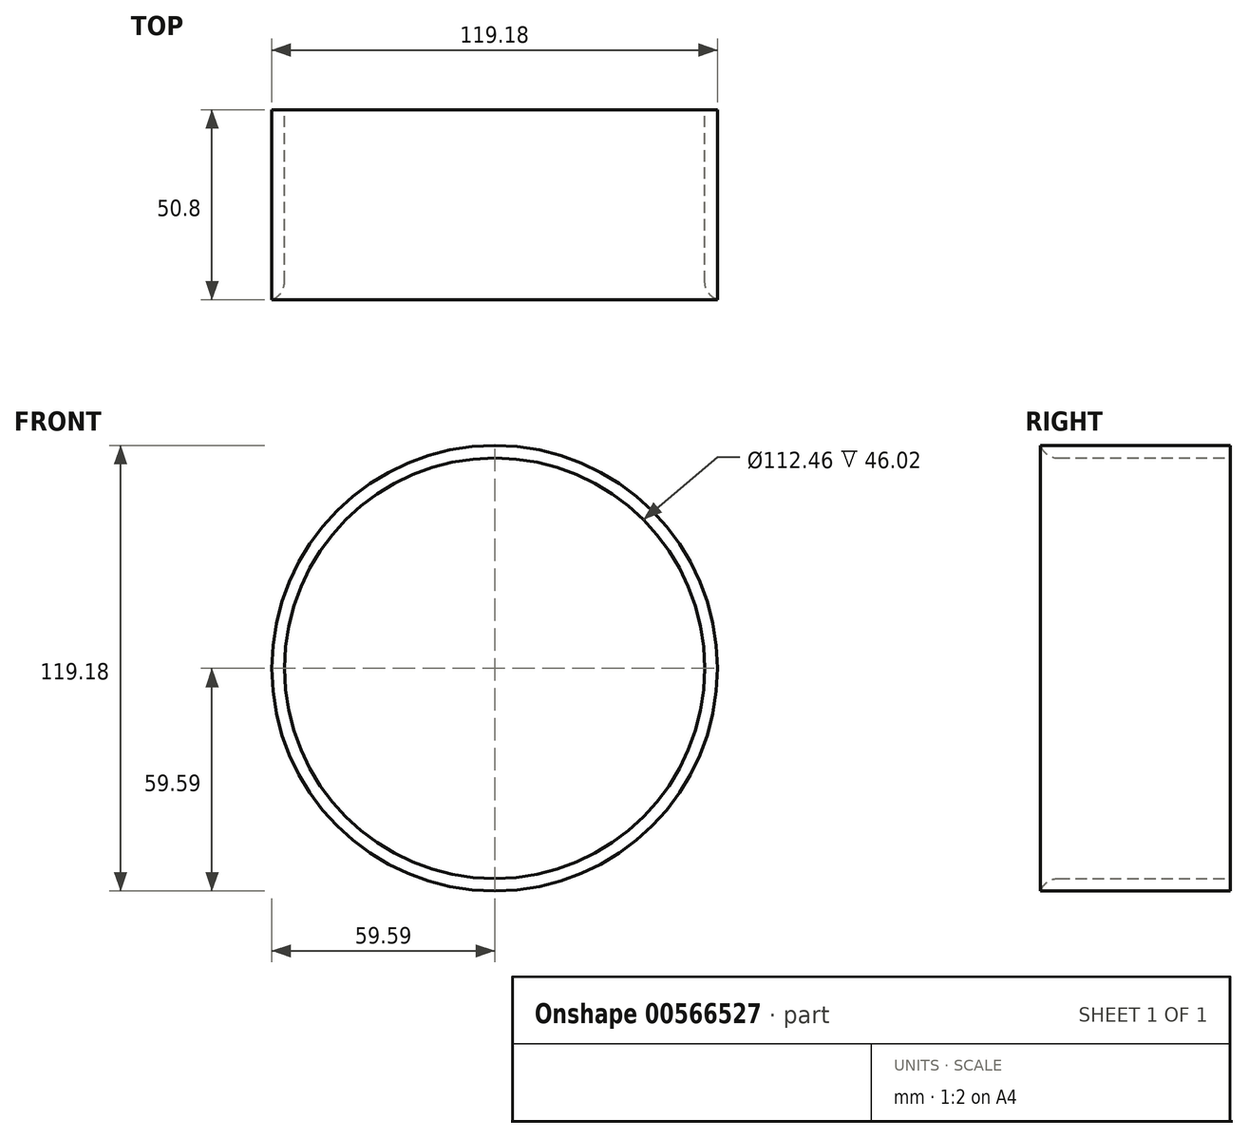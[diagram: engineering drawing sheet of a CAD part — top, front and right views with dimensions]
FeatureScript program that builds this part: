
annotation { "Feature Type Name" : "Feature", "Feature Type Description" : "" }
export const myFeature = defineFeature(function(context is Context, id is Id, definition is map)
    precondition{}
    {
        {
            var Q0;
            Q0=qCreatedBy(makeId("Front.planeOp"),FACE);
            var sketch = newSketch(context, id + "F0", { "sketchPlane" : qUnion([Q0])});
            skCircle(sketch, "E0", {"center": v(0, 0) * mm, "radius": 59.6 * mm});
            skCircle(sketch, "E1", {"center": v(0, 0) * mm, "radius": 56.23 * mm});
            skSolve(sketch);
        }
        {
            var Q0;
            Q0=makeQuery(id+"F0.imprint","IMPRINT",FACE,{"disambiguationData":[TD([[makeQuery(id+"F0.imprint","IMPRINT",EDGE,{"derivedFrom":sQuery(id+"F0.wireOp",EDGE,"E0")}),1.0]])]});
            extrude(context, id + "F1", {"entities" : qUnion([Q0]), "depth" : 50.8 * mm, "offsetDistance" : 25.4 * mm});
        }
        {
            var Q0;
            Q0=makeQuery(id+"F1.opExtrude","CAP_EDGE",EDGE,{"disambiguationData":[OSD([sQuery(id+"F0.wireOp",EDGE,"E1")])],"isStart":false});
            fillet(context, id + "F2", {"entities" : qUnion([Q0]), "radius" : 5.08 * mm, "tangentPropagation" : true, "allowEdgeOverflow" : false});
        }
    });
